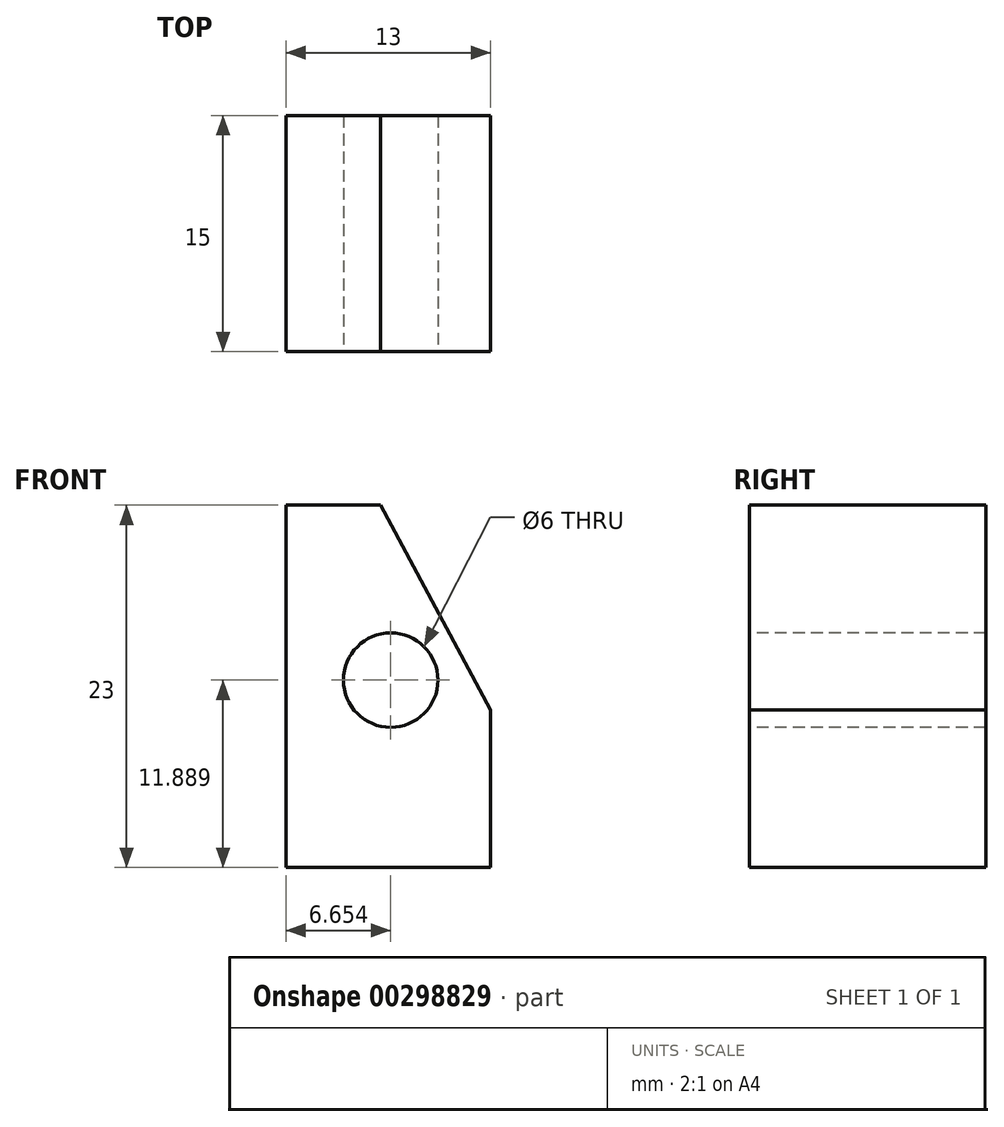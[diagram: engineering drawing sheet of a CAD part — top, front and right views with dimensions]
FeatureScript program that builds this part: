
annotation { "Feature Type Name" : "Feature", "Feature Type Description" : "" }
export const myFeature = defineFeature(function(context is Context, id is Id, definition is map)
    precondition{}
    {
        {
            var Q0;
            Q0=qCreatedBy(makeId("Front.planeOp"),FACE);
            var sketch = newSketch(context, id + "F0", { "sketchPlane" : qUnion([Q0])});
            skLineSegment(sketch, "E0", {"start": v(0, 0) * mm, "end": v(0, 23) * mm});
            skLineSegment(sketch, "E1", {"start": v(0, 0) * mm, "end": v(13, 0) * mm});
            skLineSegment(sketch, "E2", {"start": v(13, 0) * mm, "end": v(13, 10) * mm});
            skLineSegment(sketch, "E3", {"start": v(0, 23) * mm, "end": v(6, 23) * mm});
            skLineSegment(sketch, "E4", {"start": v(6, 23) * mm, "end": v(13, 10) * mm});
            skSolve(sketch);
        }
        {
            var Q0;
            Q0=makeQuery(id+"F0.imprint","IMPRINT",FACE,{"disambiguationData":[TD([[makeQuery(id+"F0.imprint","IMPRINT",EDGE,{"derivedFrom":sQuery(id+"F0.wireOp",EDGE,"E0")}),-1.0]])]});
            extrude(context, id + "F1", {"entities" : qUnion([Q0]), "depth" : 15 * mm});
        }
        {
            var Q0;
            Q0=makeQuery(id+"F1.opExtrude","CAP_FACE",FACE,{"disambiguationData":[OSD([sQuery(id+"F0.wireOp",EDGE,"E0"),sQuery(id+"F0.wireOp",EDGE,"E1"),sQuery(id+"F0.wireOp",EDGE,"E2"),sQuery(id+"F0.wireOp",EDGE,"E3"),sQuery(id+"F0.wireOp",EDGE,"E4")])],"isStart":false});
            var sketch = newSketch(context, id + "F2", { "sketchPlane" : qUnion([Q0])});
            skCircle(sketch, "E5", {"center": v(6.65, 11.89) * mm, "radius": 3.13 * mm});
            skSolve(sketch);
        }
        {
            var Q0;
            Q0=sQuery(id+"F2.wireOp",VERTEX,"E5.center");
            var Q1;
            Q1=makeQuery(id+"F1.opExtrude","SWEPT_BODY",BODY,{"disambiguationData":[OSD([sQuery(id+"F0.wireOp",EDGE,"E0"),sQuery(id+"F0.wireOp",EDGE,"E1"),sQuery(id+"F0.wireOp",EDGE,"E2"),sQuery(id+"F0.wireOp",EDGE,"E3"),sQuery(id+"F0.wireOp",EDGE,"E4")])]});
            hole(context, id + "F3", {"style" : HoleStyle.SIMPLE, "endStyle" : HoleEndStyle.THROUGH, "holeDiameter" : 6 * mm, "tappedDepth" : 12 * mm, "tapClearance" : 3, "locations" : qUnion([Q0]), "scope" : qUnion([Q1])});
        }
    });
